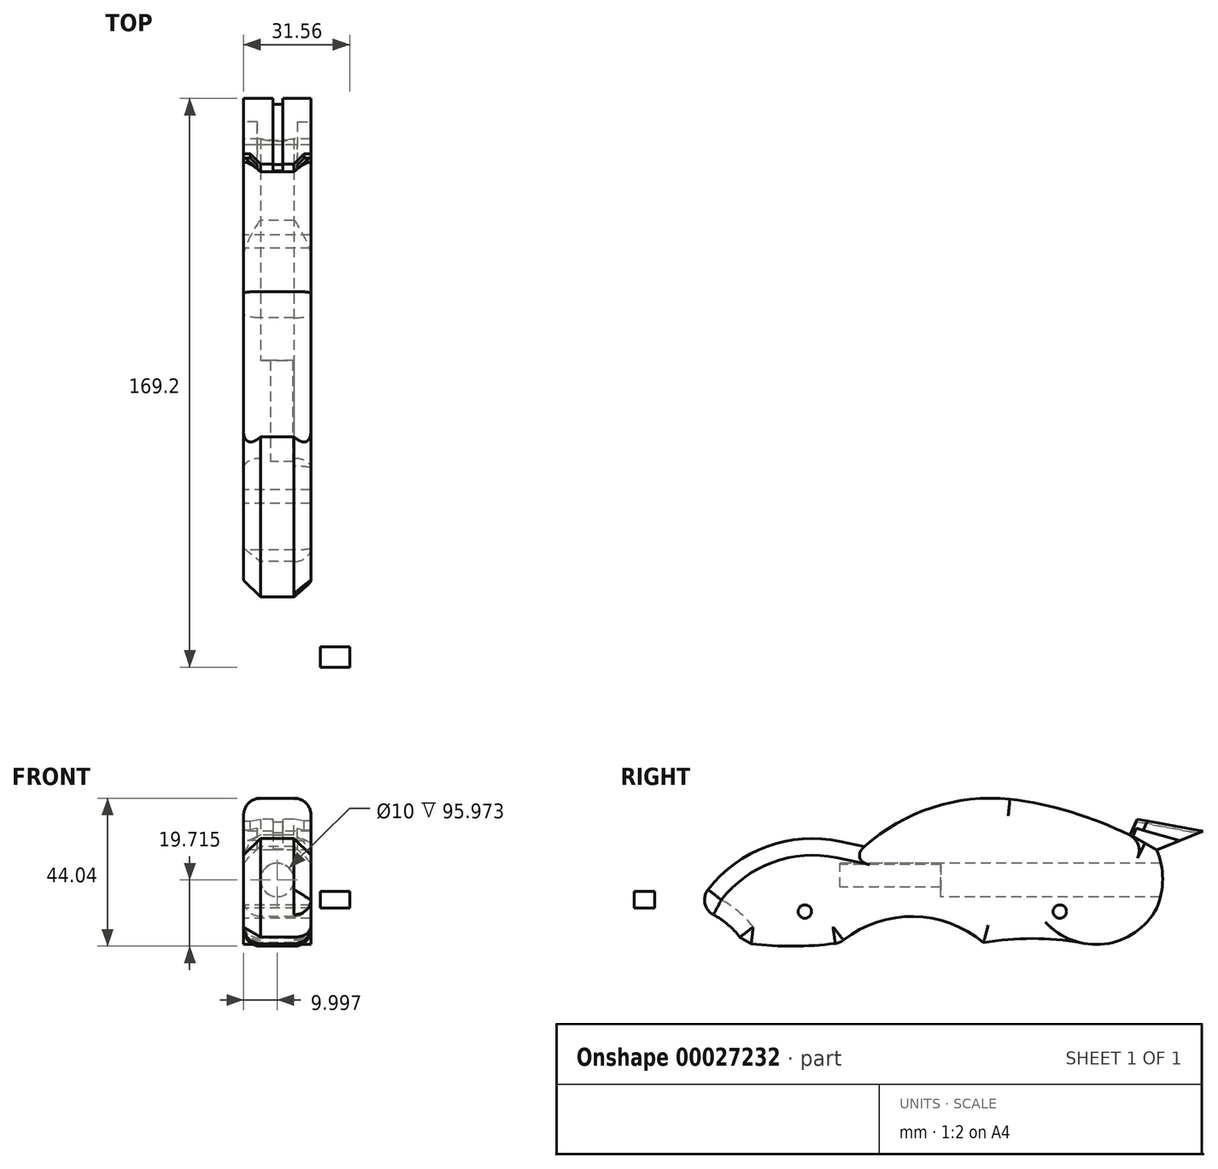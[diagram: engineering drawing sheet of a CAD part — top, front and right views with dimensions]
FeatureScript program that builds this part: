
annotation { "Feature Type Name" : "Feature", "Feature Type Description" : "" }
export const myFeature = defineFeature(function(context is Context, id is Id, definition is map)
    precondition{}
    {
        {
            var Q0;
            Q0=qCreatedBy(makeId("Right.planeOp"),FACE);
            var sketch = newSketch(context, id + "F0", { "sketchPlane" : qUnion([Q0])});
            skArc(sketch, "E0", {"start": v(0, 19.86) * mm, "mid": v(-24.72, 17.05) * mm, "end": v(-42.83, 0) * mm});
            skLineSegment(sketch, "E1", {"start": v(0, 19.86) * mm, "end": v(7.26, 18.33) * mm});
            skArc(sketch, "E2", {"start": v(50.54, 32.44) * mm, "mid": v(27.43, 29.89) * mm, "end": v(7.26, 18.33) * mm});
            skArc(sketch, "E3", {"start": v(94.2, 17.34) * mm, "mid": v(73.15, 27.14) * mm, "end": v(50.54, 32.44) * mm});
            skArc(sketch, "E4", {"start": v(94.2, 0) * mm, "mid": v(95.97, 8.67) * mm, "end": v(94.2, 17.34) * mm});
            skArc(sketch, "E5", {"start": v(71.68, -10.34) * mm, "mid": v(57.18, -9.07) * mm, "end": v(42.69, -10.34) * mm});
            skArc(sketch, "E6", {"start": v(-28.66, -10.34) * mm, "mid": v(-34.75, -3.8) * mm, "end": v(-42.83, 0) * mm});
            skArc(sketch, "E7", {"start": v(42.69, -10.34) * mm, "mid": v(21.34, -2.52) * mm, "end": v(0, -10.34) * mm});
            skArc(sketch, "E8", {"start": v(71.68, -10.34) * mm, "mid": v(84.7, -9) * mm, "end": v(94.2, 0) * mm});
            skArc(sketch, "E9", {"start": v(-28.66, -10.34) * mm, "mid": v(-14.33, -11.35) * mm, "end": v(0, -10.34) * mm});
            skCircle(sketch, "E10", {"center": v(65.38, -1.05) * mm, "radius": 2 * mm});
            skCircle(sketch, "E11", {"center": v(-10.46, -1.05) * mm, "radius": 2 * mm});
            skLineSegment(sketch, "E12", {"start": v(86.2, 21.7) * mm, "end": v(88.42, 26.45) * mm});
            skLineSegment(sketch, "E13", {"start": v(88.42, 26.45) * mm, "end": v(107.99, 22.86) * mm});
            skLineSegment(sketch, "E14", {"start": v(107.99, 22.86) * mm, "end": v(94.2, 17.34) * mm});
            skLineSegment(sketch, "E15", {"start": v(87.31, 24.07) * mm, "end": v(101.1, 20.1) * mm});
            skSolve(sketch);
        }
        {
            var Q0;
            Q0 = qSketchRegion(id + "F0", true);
            var Q1;
            Q1 = qSketchRegion(id + "FMUmQqiW1lGSUrm_1", true);
            extrude(context, id + "F1", {"entities" : qUnion([Q0, Q1]), "depth" : 20 * mm});
        }
        {
            var Q0;
            Q0=qCreatedBy(makeId("Front.planeOp"),FACE);
            var sketch = newSketch(context, id + "F2", { "sketchPlane" : qUnion([Q0])});
            skCircle(sketch, "E16", {"center": v(10, 8.36) * mm, "radius": 5 * mm});
            skPoint(sketch, "E17.orphan", {"position": v(0, 8.36) * mm});
            skPoint(sketch, "E18.start.orphan", {"position": v(19.99, 8.36) * mm});
            skSolve(sketch);
        }
        {
            var Q0;
            Q0 = qSketchRegion(id + "F2", true);
            extrude(context, id + "F3", {"entities" : qUnion([Q0]), "operationType" : NewBodyOperationType.REMOVE, "oppositeDirection" : true, "depth" : 109.74 * mm});
        }
        {
            var Q0;
            Q0=makeQuery(id+"F1.opExtrude","CAP_EDGE",EDGE,{"disambiguationData":[OSD([sQuery(id+"F0.wireOp",EDGE,"E9")])],"isStart":false});
            var Q1;
            Q1=makeQuery(id+"F1.opExtrude","CAP_EDGE",EDGE,{"disambiguationData":[OSD([sQuery(id+"F0.wireOp",EDGE,"E7")])],"isStart":false});
            var Q2;
            Q2=makeQuery(id+"F1.opExtrude","CAP_EDGE",EDGE,{"disambiguationData":[OSD([sQuery(id+"F0.wireOp",EDGE,"E5")])],"isStart":false});
            var Q3;
            Q3=makeQuery(id+"F1.opExtrude","CAP_EDGE",EDGE,{"disambiguationData":[OSD([sQuery(id+"F0.wireOp",EDGE,"E6")])],"isStart":false});
            var Q4;
            Q4=makeQuery(id+"F1.opExtrude","SWEPT_EDGE",EDGE,{"disambiguationData":[OSD([sQuery(id+"F0.wireOp",EDGE,"E0"),sQuery(id+"F0.wireOp",EDGE,"E6")])]});
            var Q5;
            Q5=makeQuery(id+"F1.opExtrude","CAP_EDGE",EDGE,{"disambiguationData":[OSD([sQuery(id+"F0.wireOp",EDGE,"E7")])],"isStart":true});
            var Q6;
            Q6=makeQuery(id+"F1.opExtrude","CAP_EDGE",EDGE,{"disambiguationData":[OSD([sQuery(id+"F0.wireOp",EDGE,"E5")])],"isStart":true});
            fillet(context, id + "F4", {"entities" : qUnion([Q0, Q1, Q2, Q3, Q4, Q5, Q6]), "radius" : 5 * mm, "tangentPropagation" : true, "allowEdgeOverflow" : false});
        }
        {
            var Q0;
            Q0=makeQuery(id+"F1.opExtrude","CAP_EDGE",EDGE,{"disambiguationData":[OSD([sQuery(id+"F0.wireOp",EDGE,"E9")])],"isStart":true});
            fillet(context, id + "F5", {"entities" : qUnion([Q0]), "radius" : 5 * mm, "tangentPropagation" : true, "allowEdgeOverflow" : false});
        }
        {
            var Q0;
            Q0=makeQuery(id+"F1.opExtrude","CAP_EDGE",EDGE,{"disambiguationData":[OSD([sQuery(id+"F0.wireOp",EDGE,"E0")])],"isStart":false});
            var Q1;
            Q1=makeQuery(id+"F1.opExtrude","CAP_EDGE",EDGE,{"disambiguationData":[OSD([sQuery(id+"F0.wireOp",EDGE,"E0")])],"isStart":true});
            chamfer(context, id + "F6", {"entities" : qUnion([Q0, Q1]), "width" : 5 * mm, "tangentPropagation" : true});
        }
        {
            var Q0;
            Q0=makeQuery(id+"F1.opExtrude","CAP_EDGE",EDGE,{"disambiguationData":[OSD([sQuery(id+"F0.wireOp",EDGE,"E2")])],"isStart":false});
            var Q1;
            Q1=makeQuery(id+"F1.opExtrude","CAP_EDGE",EDGE,{"disambiguationData":[OSD([sQuery(id+"F0.wireOp",EDGE,"E2")])],"isStart":true});
            fillet(context, id + "F7", {"entities" : qUnion([Q0, Q1]), "radius" : 5 * mm, "tangentPropagation" : true, "allowEdgeOverflow" : false});
        }
        {
            var Q0;
            Q0=qCreatedBy(makeId("Front.planeOp"),FACE);
            var sketch = newSketch(context, id + "F8", { "sketchPlane" : qUnion([Q0])});
            skCircle(sketch, "E19", {"center": v(9.88, 8.26) * mm, "radius": 5.06 * mm});
            skSolve(sketch);
        }
        {
            var Q0;
            Q0 = qSketchRegion(id + "F8", true);
            extrude(context, id + "F9", {"entities" : qUnion([Q0]), "operationType" : NewBodyOperationType.ADD, "oppositeDirection" : true, "depth" : 30 * mm});
        }
        {
            var Q0;
            {var subQ2=sQuery(id+"F0.wireOp",EDGE,"E13");Q0=makeQuery(id+"F0.imprint","IMPRINT",FACE,{"disambiguationData":[TD([[makeQuery(id+"F0.imprint","IMPRINT",EDGE,{"derivedFrom":subQ2}),-1.0]])]});}
            extrude(context, id + "F10", {"entities" : qUnion([Q0]), "operationType" : NewBodyOperationType.REMOVE, "depth" : 2 * mm});
        }
        {
            var Q0;
            {var subQ0=sQuery(id+"F0.wireOp",EDGE,"E15");Q0=makeQuery(id+"F0.imprint","IMPRINT",FACE,{"disambiguationData":[TD([[makeQuery(id+"F0.imprint","IMPRINT",EDGE,{"derivedFrom":subQ0}),-1.0]])]});}
            extrude(context, id + "F11", {"entities" : qUnion([Q0]), "operationType" : NewBodyOperationType.REMOVE, "depth" : 4.06 * mm});
        }
        {
            var Q0;
            Q0=makeQuery(id+"F1.opExtrude","CAP_FACE",FACE,{"disambiguationData":[OSD([sQuery(id+"F0.wireOp",EDGE,"E0"),sQuery(id+"F0.wireOp",EDGE,"E1"),sQuery(id+"F0.wireOp",EDGE,"E2"),sQuery(id+"F0.wireOp",EDGE,"E3"),sQuery(id+"F0.wireOp",EDGE,"E4"),sQuery(id+"F0.wireOp",EDGE,"E5"),sQuery(id+"F0.wireOp",EDGE,"E6"),sQuery(id+"F0.wireOp",EDGE,"E7"),sQuery(id+"F0.wireOp",EDGE,"E8"),sQuery(id+"F0.wireOp",EDGE,"E9"),sQuery(id+"F0.wireOp",EDGE,"E10"),sQuery(id+"F0.wireOp",EDGE,"E11"),sQuery(id+"F0.wireOp",EDGE,"E12"),sQuery(id+"F0.wireOp",EDGE,"E13"),sQuery(id+"F0.wireOp",EDGE,"E14")])],"isStart":false});
            var sketch = newSketch(context, id + "F12", { "sketchPlane" : qUnion([Q0])});
            skLineSegment(sketch, "E20", {"start": v(88.42, 26.45) * mm, "end": v(107.99, 22.86) * mm});
            skPoint(sketch, "E21.orphan", {"position": v(84.08, 17.16) * mm});
            skLineSegment(sketch, "E22", {"start": v(107.99, 22.86) * mm, "end": v(101.1, 20.1) * mm});
            skLineSegment(sketch, "E23", {"start": v(101.1, 20.1) * mm, "end": v(87.25, 23.95) * mm});
            skLineSegment(sketch, "E24", {"start": v(87.25, 23.95) * mm, "end": v(88.42, 26.45) * mm});
            skLineSegment(sketch, "E25", {"start": v(86.25, 21.8) * mm, "end": v(94.2, 17.34) * mm});
            skSolve(sketch);
        }
        {
            var Q0;
            {var subQ2=sQuery(id+"F12.wireOp",EDGE,"E20");Q0=makeQuery(id+"F12.imprint","IMPRINT",FACE,{"disambiguationData":[TD([[makeQuery(id+"F12.imprint","IMPRINT",EDGE,{"derivedFrom":subQ2}),-1.0]])]});}
            extrude(context, id + "F13", {"entities" : qUnion([Q0]), "operationType" : NewBodyOperationType.REMOVE, "oppositeDirection" : true, "depth" : 2 * mm});
        }
        {
            var Q0;
            Q0=makeQuery(id+"F12.imprint","IMPRINT",FACE,{"disambiguationData":[TD([[makeQuery(id+"F12.imprint","IMPRINT",EDGE,{"derivedFrom":sQuery(id+"F12.wireOp",EDGE,"E20")}),-1.0]])]});
            extrude(context, id + "F14", {"entities" : qUnion([Q0]), "operationType" : NewBodyOperationType.REMOVE, "oppositeDirection" : true, "depth" : 2 * mm});
        }
        {
            var Q0;
            {var subQ2=sQuery(id+"F12.wireOp",EDGE,"E23");Q0=makeQuery(id+"F12.imprint","IMPRINT",FACE,{"disambiguationData":[TD([[makeQuery(id+"F12.imprint","IMPRINT",EDGE,{"derivedFrom":subQ2}),1.0]])]});}
            extrude(context, id + "F15", {"entities" : qUnion([Q0]), "operationType" : NewBodyOperationType.REMOVE, "oppositeDirection" : true, "depth" : 4.06 * mm});
        }
        {
            var Q0;
            Q0=makeQuery(id+"F1.opExtrude","CAP_EDGE",EDGE,{"disambiguationData":[OSD([sQuery(id+"F0.wireOp",EDGE,"E12")])],"isStart":false});
            var Q1;
            Q1=makeQuery(id+"F1.opExtrude","CAP_EDGE",EDGE,{"disambiguationData":[OSD([sQuery(id+"F0.wireOp",EDGE,"E12")])],"isStart":true});
            chamfer(context, id + "F16", {"entities" : qUnion([Q0, Q1]), "width" : 5 * mm, "tangentPropagation" : true});
        }
        {
            var Q0;
            Q0=makeQuery(id+"F1.opExtrude","SWEPT_FACE",FACE,{"disambiguationData":[OSD([sQuery(id+"F0.wireOp",EDGE,"E13")])]});
            var sketch = newSketch(context, id + "F17", { "sketchPlane" : qUnion([Q0])});
            skLineSegment(sketch, "E26", {"start": v(15, 82.18) * mm, "end": v(5, 82.18) * mm});
            skLineSegment(sketch, "E27", {"start": v(8.71, 82.18) * mm, "end": v(8.71, 102.07) * mm});
            skLineSegment(sketch, "E28", {"start": v(8.71, 102.07) * mm, "end": v(10, 102.07) * mm});
            skLineSegment(sketch, "E29", {"start": v(10, 102.07) * mm, "end": v(10, 82.18) * mm});
            skLineSegment(sketch, "E30", {"start": v(10, 82.18) * mm, "end": v(8.71, 82.18) * mm});
            skSolve(sketch);
        }
        {
            var Q0;
            Q0=makeQuery(id+"F1.opExtrude","SWEPT_FACE",FACE,{"disambiguationData":[OSD([sQuery(id+"F0.wireOp",EDGE,"E14")])]});
            var sketch = newSketch(context, id + "F18", { "sketchPlane" : qUnion([Q0])});
            skLineSegment(sketch, "E31", {"start": v(10, -108.75) * mm, "end": v(10, -93.9) * mm});
            skLineSegment(sketch, "E32", {"start": v(8.66, -108.75) * mm, "end": v(8.66, -93.9) * mm});
            skLineSegment(sketch, "E33", {"start": v(8.66, -93.9) * mm, "end": v(10, -93.9) * mm});
            skLineSegment(sketch, "E34", {"start": v(10, -108.75) * mm, "end": v(8.66, -108.75) * mm});
            skSolve(sketch);
        }
        {
            var Q0;
            Q0=makeQuery(id+"F1.opExtrude","SWEPT_FACE",FACE,{"disambiguationData":[OSD([sQuery(id+"F0.wireOp",EDGE,"E12")])]});
            var sketch = newSketch(context, id + "F19", { "sketchPlane" : qUnion([Q0])});
            skLineSegment(sketch, "E35", {"start": v(8.73, 61.4) * mm, "end": v(8.73, 56.14) * mm});
            skLineSegment(sketch, "E36", {"start": v(10, 61.4) * mm, "end": v(10, 56.14) * mm});
            skLineSegment(sketch, "E37", {"start": v(10, 56.14) * mm, "end": v(8.73, 56.14) * mm});
            skLineSegment(sketch, "E38", {"start": v(10, 61.4) * mm, "end": v(8.73, 61.4) * mm});
            skSolve(sketch);
        }
        {
            var Q0;
            Q0 = qSketchRegion(id + "F17", true);
            extrude(context, id + "F20", {"entities" : qUnion([Q0]), "operationType" : NewBodyOperationType.REMOVE, "oppositeDirection" : true, "depth" : 0.82 * mm});
        }
        {
            var Q0;
            Q0 = qSketchRegion(id + "F19", true);
            extrude(context, id + "F21", {"entities" : qUnion([Q0]), "operationType" : NewBodyOperationType.REMOVE, "oppositeDirection" : true, "depth" : 0.3 * mm});
        }
        {
            var Q0;
            Q0=makeQuery(id+"F21.boolean.opBoolean","MERGE",FACE,{"derivedFrom":[makeQuery(id+"F20.boolean.opBoolean","COPY",FACE,{"derivedFrom":makeQuery(id+"F20.opExtrude","SWEPT_FACE",FACE,{"disambiguationData":[OSD([sQuery(id+"F17.wireOp",EDGE,"E29")])]})}),makeQuery(id+"F21.opExtrude","SWEPT_FACE",FACE,{"disambiguationData":[OSD([sQuery(id+"F19.wireOp",EDGE,"E36")])]})]});
            extrude(context, id + "F22", {"entities" : qUnion([Q0]), "operationType" : NewBodyOperationType.REMOVE, "oppositeDirection" : true, "depth" : 1.6 * mm});
        }
        {
            var Q0;
            Q0 = qSketchRegion(id + "F18", true);
            extrude(context, id + "F23", {"entities" : qUnion([Q0]), "operationType" : NewBodyOperationType.REMOVE, "oppositeDirection" : true, "depth" : 0.16 * mm});
        }
        {
            var Q0;
            Q0=makeQuery(id+"F23.boolean.opBoolean","COPY",FACE,{"derivedFrom":makeQuery(id+"F23.opExtrude","SWEPT_FACE",FACE,{"disambiguationData":[OSD([sQuery(id+"F18.wireOp",EDGE,"E31")])]})});
            extrude(context, id + "F24", {"entities" : qUnion([Q0]), "operationType" : NewBodyOperationType.REMOVE, "oppositeDirection" : true, "depth" : 1.6 * mm});
        }
        {
            var Q0;
            Q0=qCreatedBy(makeId("Top.planeOp"),FACE);
            var sketch = newSketch(context, id + "F25", { "sketchPlane" : qUnion([Q0])});
            skLineSegment(sketch, "E39.bottom", {"start": v(31.56, -61.2) * mm, "end": v(22.8, -61.2) * mm});
            skLineSegment(sketch, "E39.top", {"start": v(31.56, -55.15) * mm, "end": v(22.8, -55.15) * mm});
            skLineSegment(sketch, "E39.left", {"start": v(31.56, -61.2) * mm, "end": v(31.56, -55.15) * mm});
            skLineSegment(sketch, "E39.right", {"start": v(22.8, -61.2) * mm, "end": v(22.8, -55.15) * mm});
            skSolve(sketch);
        }
        {
            var Q0;
            Q0=makeQuery(id+"F25.imprint","IMPRINT",FACE,{"disambiguationData":[TD([[makeQuery(id+"F25.imprint","IMPRINT",EDGE,{"derivedFrom":sQuery(id+"F25.wireOp",EDGE,"E39.bottom")}),-1.0]])]});
            extrude(context, id + "F26", {"entities" : qUnion([Q0]), "depth" : 5 * mm});
        }
        {
            var Q0;
            Q0=makeQuery(id+"F13.boolean.opBoolean","COPY",FACE,{"derivedFrom":makeQuery(id+"F13.opExtrude","CAP_FACE",FACE,{"disambiguationData":[OSD([sQuery(id+"F12.wireOp",EDGE,"E20"),sQuery(id+"F12.wireOp",EDGE,"E22"),sQuery(id+"F12.wireOp",EDGE,"E23"),sQuery(id+"F12.wireOp",EDGE,"E24")])],"isStart":false})});
            var Q1;
            Q1=makeQuery(id+"F1.opExtrude","CAP_FACE",FACE,{"disambiguationData":[OSD([sQuery(id+"F0.wireOp",EDGE,"E0"),sQuery(id+"F0.wireOp",EDGE,"E1"),sQuery(id+"F0.wireOp",EDGE,"E2"),sQuery(id+"F0.wireOp",EDGE,"E3"),sQuery(id+"F0.wireOp",EDGE,"E4"),sQuery(id+"F0.wireOp",EDGE,"E5"),sQuery(id+"F0.wireOp",EDGE,"E6"),sQuery(id+"F0.wireOp",EDGE,"E7"),sQuery(id+"F0.wireOp",EDGE,"E8"),sQuery(id+"F0.wireOp",EDGE,"E9"),sQuery(id+"F0.wireOp",EDGE,"E10"),sQuery(id+"F0.wireOp",EDGE,"E11"),sQuery(id+"F0.wireOp",EDGE,"E12"),sQuery(id+"F0.wireOp",EDGE,"E13"),sQuery(id+"F0.wireOp",EDGE,"E14")])],"isStart":false});
            extrude(context, id + "F27", {"entities" : qUnion([Q0]), "operationType" : NewBodyOperationType.ADD, "endBound" : BoundingType.UP_TO_SURFACE, "endBoundEntityFace" : qUnion([Q1]), "depth" : 25 * mm});
        }
        {
            var Q0;
            Q0=makeQuery(id+"F10.boolean.opBoolean","COPY",FACE,{"derivedFrom":makeQuery(id+"F10.opExtrude","CAP_FACE",FACE,{"disambiguationData":[OSD([sQuery(id+"F0.wireOp",EDGE,"E12"),sQuery(id+"F0.wireOp",EDGE,"E13"),sQuery(id+"F0.wireOp",EDGE,"E14"),sQuery(id+"F0.wireOp",EDGE,"E15")])],"isStart":false})});
            var Q1;
            Q1=makeQuery(id+"F1.opExtrude","CAP_FACE",FACE,{"disambiguationData":[OSD([sQuery(id+"F0.wireOp",EDGE,"E0"),sQuery(id+"F0.wireOp",EDGE,"E1"),sQuery(id+"F0.wireOp",EDGE,"E2"),sQuery(id+"F0.wireOp",EDGE,"E3"),sQuery(id+"F0.wireOp",EDGE,"E4"),sQuery(id+"F0.wireOp",EDGE,"E5"),sQuery(id+"F0.wireOp",EDGE,"E6"),sQuery(id+"F0.wireOp",EDGE,"E7"),sQuery(id+"F0.wireOp",EDGE,"E8"),sQuery(id+"F0.wireOp",EDGE,"E9"),sQuery(id+"F0.wireOp",EDGE,"E10"),sQuery(id+"F0.wireOp",EDGE,"E11"),sQuery(id+"F0.wireOp",EDGE,"E12"),sQuery(id+"F0.wireOp",EDGE,"E13"),sQuery(id+"F0.wireOp",EDGE,"E14")])],"isStart":true});
            extrude(context, id + "F28", {"entities" : qUnion([Q0]), "operationType" : NewBodyOperationType.ADD, "endBound" : BoundingType.UP_TO_SURFACE, "endBoundEntityFace" : qUnion([Q1]), "depth" : 25 * mm});
        }
    });
